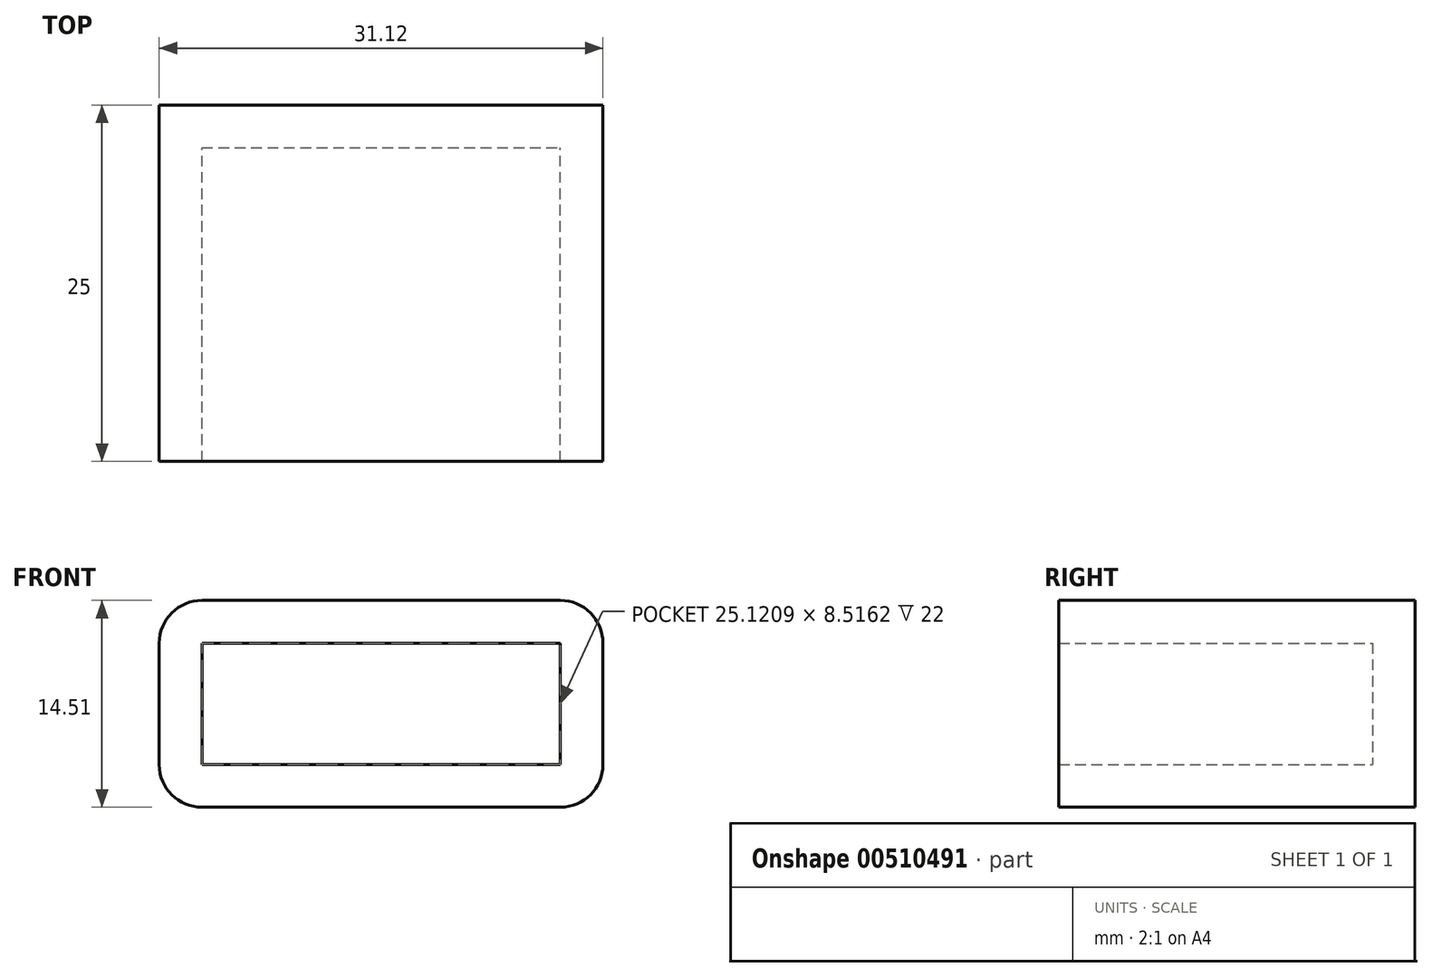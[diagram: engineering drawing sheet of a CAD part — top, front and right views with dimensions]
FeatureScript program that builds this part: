
annotation { "Feature Type Name" : "Feature", "Feature Type Description" : "" }
export const myFeature = defineFeature(function(context is Context, id is Id, definition is map)
    precondition{}
    {
        {
            var Q0;
            Q0=qCreatedBy(makeId("Front.planeOp"),FACE);
            var sketch = newSketch(context, id + "F0", { "sketchPlane" : qUnion([Q0])});
            skLineSegment(sketch, "E0.bottom", {"start": v(-55.43, 35.38) * mm, "end": v(-30.3, 35.38) * mm});
            skLineSegment(sketch, "E0.top", {"start": v(-55.43, 20.87) * mm, "end": v(-30.3, 20.87) * mm});
            skLineSegment(sketch, "E0.left", {"start": v(-58.43, 32.38) * mm, "end": v(-58.43, 23.87) * mm});
            skLineSegment(sketch, "E0.right", {"start": v(-27.3, 32.38) * mm, "end": v(-27.3, 23.87) * mm});
            skPoint(sketch, "E1.visualSharp", {"position": v(-27.3, 35.38) * mm});
            skArc(sketch, "E1.filletArc", {"start": v(-27.3, 32.38) * mm, "mid": v(-28.19, 34.5) * mm, "end": v(-30.3, 35.38) * mm});
            skPoint(sketch, "E2.visualSharp", {"position": v(-27.3, 20.87) * mm});
            skArc(sketch, "E2.filletArc", {"start": v(-30.3, 20.87) * mm, "mid": v(-28.19, 21.75) * mm, "end": v(-27.3, 23.87) * mm});
            skPoint(sketch, "E3.visualSharp", {"position": v(-58.43, 20.87) * mm});
            skArc(sketch, "E3.filletArc", {"start": v(-58.43, 23.87) * mm, "mid": v(-57.55, 21.75) * mm, "end": v(-55.43, 20.87) * mm});
            skPoint(sketch, "E4.visualSharp", {"position": v(-58.43, 35.38) * mm});
            skArc(sketch, "E4.filletArc", {"start": v(-55.43, 35.38) * mm, "mid": v(-57.55, 34.5) * mm, "end": v(-58.43, 32.38) * mm});
            skSolve(sketch);
        }
        {
            var Q0;
            Q0 = qSketchRegion(id + "F0", true);
            extrude(context, id + "F1", {"entities" : qUnion([Q0]), "depth" : 25 * mm});
        }
        {
            var Q0;
            Q0=makeQuery(id+"F1.opExtrude","CAP_FACE",FACE,{"disambiguationData":[OSD([sQuery(id+"F0.wireOp",EDGE,"E0.bottom"),sQuery(id+"F0.wireOp",EDGE,"E0.top"),sQuery(id+"F0.wireOp",EDGE,"E0.left"),sQuery(id+"F0.wireOp",EDGE,"E0.right"),sQuery(id+"F0.wireOp",EDGE,"E1.filletArc"),sQuery(id+"F0.wireOp",EDGE,"E2.filletArc"),sQuery(id+"F0.wireOp",EDGE,"E3.filletArc"),sQuery(id+"F0.wireOp",EDGE,"E4.filletArc")])],"isStart":false});
            shell(context, id + "F2", {"entities" : qUnion([Q0]), "thickness" : 3 * mm});
        }
    });
